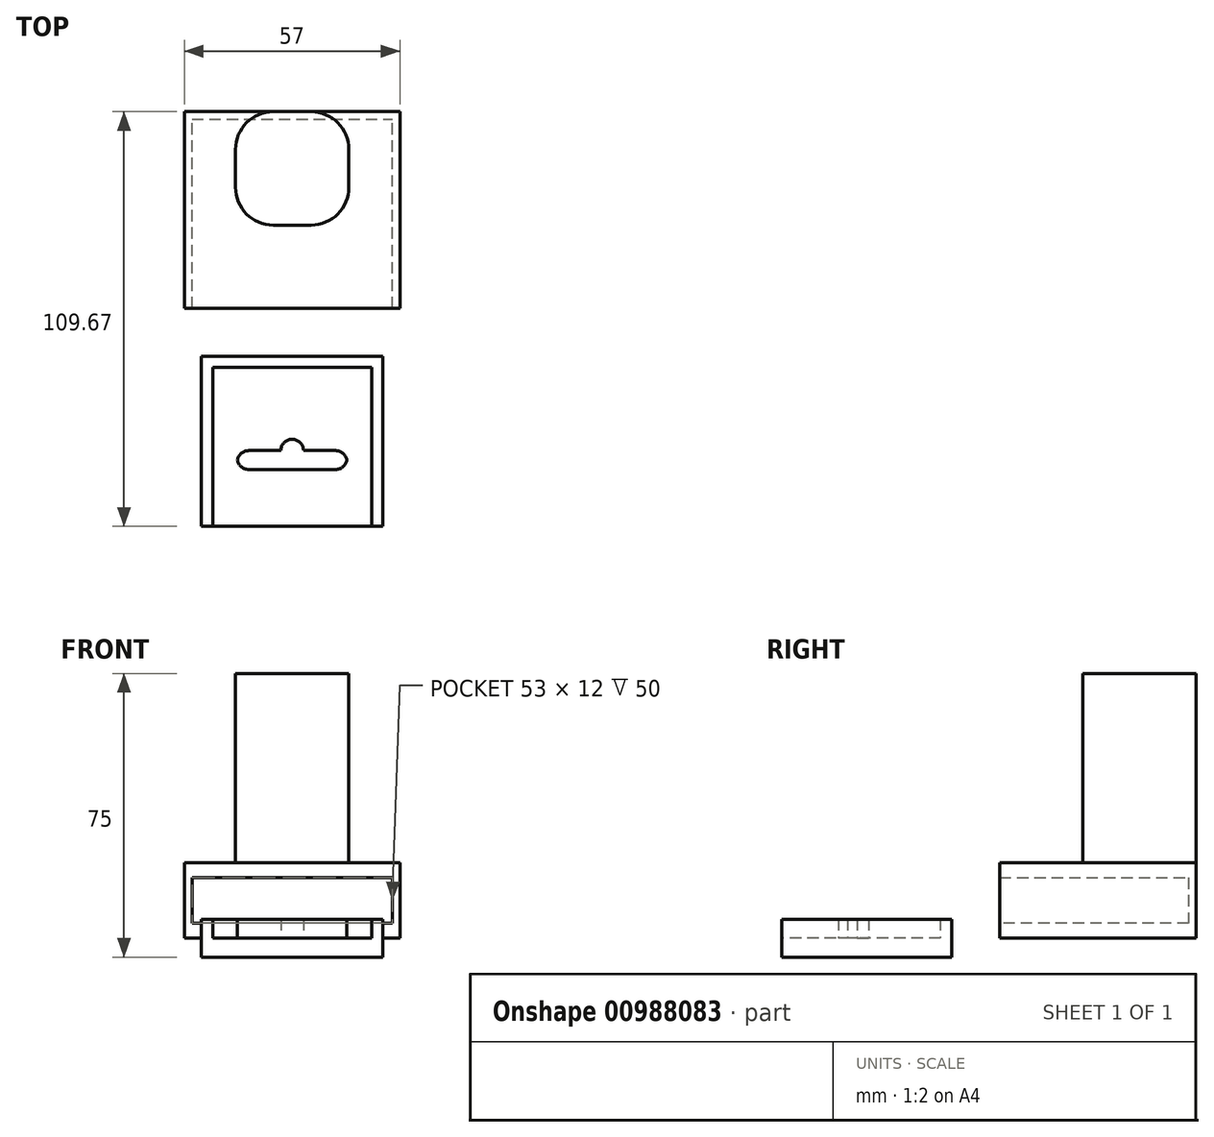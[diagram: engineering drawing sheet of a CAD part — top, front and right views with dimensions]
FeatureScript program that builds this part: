
annotation { "Feature Type Name" : "Feature", "Feature Type Description" : "" }
export const myFeature = defineFeature(function(context is Context, id is Id, definition is map)
    precondition{}
    {
        {
            var Q0;
            Q0=qCreatedBy(makeId("Top.planeOp"),FACE);
            var sketch = newSketch(context, id + "F0", { "sketchPlane" : qUnion([Q0])});
            skLineSegment(sketch, "E0.bottom", {"start": v(21, 19.5) * mm, "end": v(-21, 19.5) * mm});
            skLineSegment(sketch, "E0.top", {"start": v(21, -19.5) * mm, "end": v(-21, -19.5) * mm});
            skLineSegment(sketch, "E0.left", {"start": v(21, 19.5) * mm, "end": v(21, -19.5) * mm});
            skLineSegment(sketch, "E0.right", {"start": v(-21, 19.5) * mm, "end": v(-21, -19.5) * mm});
            skPoint(sketch, "E0.middle", {"position": v(0, 0) * mm});
            skLineSegment(sketch, "E1.bottom", {"start": v(-14.5, -2.5) * mm, "end": v(-3, -2.5) * mm});
            skLineSegment(sketch, "E1.top", {"start": v(-14.5, -7.5) * mm, "end": v(14.5, -7.5) * mm});
            skLineSegment(sketch, "E1.left", {"start": v(-14.5, -2.5) * mm, "end": v(-14.5, -7.5) * mm});
            skLineSegment(sketch, "E1.right", {"start": v(14.5, -2.5) * mm, "end": v(14.5, -7.5) * mm});
            skPoint(sketch, "E2", {"position": v(0, -2.5) * mm});
            skLineSegment(sketch, "E3.bottom", {"start": v(-3, -7.5) * mm, "end": v(3, -7.5) * mm});
            skLineSegment(sketch, "E3.top", {"start": v(-3, 0.5) * mm, "end": v(3, 0.5) * mm});
            skLineSegment(sketch, "E3.left", {"start": v(-3, -2.5) * mm, "end": v(-3, 0.5) * mm});
            skLineSegment(sketch, "E3.right", {"start": v(3, -2.5) * mm, "end": v(3, 0.5) * mm});
            skPoint(sketch, "E4", {"position": v(0, 0.5) * mm});
            skLineSegment(sketch, "E5.trimOffspring", {"start": v(3, -2.5) * mm, "end": v(14.5, -2.5) * mm});
            skLineSegment(sketch, "E6.0", {"start": v(24, 22.5) * mm, "end": v(-24, 22.5) * mm});
            skLineSegment(sketch, "E6.1", {"start": v(24, 22.5) * mm, "end": v(24, -22.5) * mm});
            skLineSegment(sketch, "E6.2", {"start": v(24, -22.5) * mm, "end": v(-24, -22.5) * mm});
            skLineSegment(sketch, "E6.3", {"start": v(-24, 22.5) * mm, "end": v(-24, -22.5) * mm});
            skLineSegment(sketch, "E7", {"start": v(-21, -19.5) * mm, "end": v(-21, -22.5) * mm});
            skLineSegment(sketch, "E8", {"start": v(21, -19.5) * mm, "end": v(21, -22.5) * mm});
            skLineSegment(sketch, "E9.bottom", {"start": v(28.5, 87.17) * mm, "end": v(-28.5, 87.17) * mm});
            skLineSegment(sketch, "E9.top", {"start": v(28.5, 35.17) * mm, "end": v(-28.5, 35.17) * mm});
            skLineSegment(sketch, "E9.left", {"start": v(28.5, 87.17) * mm, "end": v(28.5, 35.17) * mm});
            skLineSegment(sketch, "E9.right", {"start": v(-28.5, 87.17) * mm, "end": v(-28.5, 35.17) * mm});
            skPoint(sketch, "E9.middle", {"position": v(0, 61.17) * mm});
            skLineSegment(sketch, "E10.0", {"start": v(-26.5, 85.17) * mm, "end": v(-26.5, 35.17) * mm});
            skLineSegment(sketch, "E10.1", {"start": v(26.5, 85.17) * mm, "end": v(-26.5, 85.17) * mm});
            skLineSegment(sketch, "E10.2", {"start": v(26.5, 85.17) * mm, "end": v(26.5, 35.17) * mm});
            skSolve(sketch);
        }
        {
            var Q0;
            Q0=makeQuery(id+"F0.imprint","IMPRINT",FACE,{"disambiguationData":[TD([[makeQuery(id+"F0.imprint","IMPRINT",EDGE,{"derivedFrom":sQuery(id+"F0.wireOp",EDGE,"E0.bottom")}),1.0]])]});
            var Q1;
            Q1=makeQuery(id+"F0.imprint","IMPRINT",FACE,{"disambiguationData":[TD([[makeQuery(id+"F0.imprint","IMPRINT",EDGE,{"derivedFrom":sQuery(id+"F0.wireOp",EDGE,"E0.bottom")}),-1.0]])]});
            var Q2;
            Q2=makeQuery(id+"F0.imprint","IMPRINT",FACE,{"disambiguationData":[TD([[makeQuery(id+"F0.imprint","IMPRINT",EDGE,{"derivedFrom":sQuery(id+"F0.wireOp",EDGE,"E0.top")}),1.0]])]});
            var Q3;
            Q3=makeQuery(id+"F0.imprint","IMPRINT",FACE,{"disambiguationData":[TD([[makeQuery(id+"F0.imprint","IMPRINT",EDGE,{"derivedFrom":sQuery(id+"F0.wireOp",EDGE,"E1.bottom")}),-1.0]])]});
            extrude(context, id + "F1", {"entities" : qUnion([Q0, Q1, Q2, Q3]), "oppositeDirection" : true, "depth" : 5 * mm, "offsetDistance" : 25 * mm});
        }
        {
            var Q0;
            Q0=makeQuery(id+"F0.imprint","IMPRINT",FACE,{"disambiguationData":[TD([[makeQuery(id+"F0.imprint","IMPRINT",EDGE,{"derivedFrom":sQuery(id+"F0.wireOp",EDGE,"E1.bottom")}),-1.0]])]});
            var Q1;
            Q1=makeQuery(id+"F0.imprint","IMPRINT",FACE,{"disambiguationData":[TD([[makeQuery(id+"F0.imprint","IMPRINT",EDGE,{"derivedFrom":sQuery(id+"F0.wireOp",EDGE,"E0.bottom")}),-1.0]])]});
            extrude(context, id + "F2", {"entities" : qUnion([Q0, Q1]), "operationType" : NewBodyOperationType.ADD, "depth" : 5 * mm, "offsetDistance" : 25 * mm});
        }
        {
            var Q0;
            Q0=makeQuery(id+"F2.opExtrude","SWEPT_EDGE",EDGE,{"disambiguationData":[OSD([sQuery(id+"F0.wireOp",EDGE,"E3.top"),sQuery(id+"F0.wireOp",EDGE,"E3.left")])]});
            var Q1;
            Q1=makeQuery(id+"F2.opExtrude","SWEPT_EDGE",EDGE,{"disambiguationData":[OSD([sQuery(id+"F0.wireOp",EDGE,"E3.top"),sQuery(id+"F0.wireOp",EDGE,"E3.right")])]});
            var Q2;
            Q2=makeQuery(id+"F2.opExtrude","SWEPT_EDGE",EDGE,{"disambiguationData":[OSD([sQuery(id+"F0.wireOp",EDGE,"E1.bottom"),sQuery(id+"F0.wireOp",EDGE,"E1.left")])]});
            var Q3;
            Q3=makeQuery(id+"F2.opExtrude","SWEPT_EDGE",EDGE,{"disambiguationData":[OSD([sQuery(id+"F0.wireOp",EDGE,"E1.top"),sQuery(id+"F0.wireOp",EDGE,"E1.left")])]});
            var Q4;
            Q4=makeQuery(id+"F2.opExtrude","SWEPT_EDGE",EDGE,{"disambiguationData":[OSD([sQuery(id+"F0.wireOp",EDGE,"E1.right"),sQuery(id+"F0.wireOp",EDGE,"E5.trimOffspring")])]});
            var Q5;
            Q5=makeQuery(id+"F2.opExtrude","SWEPT_EDGE",EDGE,{"disambiguationData":[OSD([sQuery(id+"F0.wireOp",EDGE,"E1.top"),sQuery(id+"F0.wireOp",EDGE,"E1.right")])]});
            fillet(context, id + "F3", {"entities" : qUnion([Q0, Q1, Q2, Q3, Q4, Q5]), "radius" : 3 * mm, "tangentPropagation" : true, "allowEdgeOverflow" : false});
        }
        {
            var Q0;
            Q0=makeQuery(id+"F0.imprint","IMPRINT",FACE,{"disambiguationData":[TD([[makeQuery(id+"F0.imprint","IMPRINT",EDGE,{"derivedFrom":sQuery(id+"F0.wireOp",EDGE,"E9.bottom")}),1.0]])]});
            extrude(context, id + "F4", {"entities" : qUnion([Q0]), "depth" : 20 * mm, "offsetDistance" : 25 * mm});
        }
        {
            var Q0;
            {var subQ0=sQuery(id+"F0.wireOp",EDGE,"E10.0");Q0=makeQuery(id+"F0.imprint","IMPRINT",FACE,{"disambiguationData":[TD([[makeQuery(id+"F0.imprint","IMPRINT",EDGE,{"derivedFrom":subQ0}),1.0]])]});}
            extrude(context, id + "F5", {"entities" : qUnion([Q0]), "operationType" : NewBodyOperationType.ADD, "depth" : 4 * mm, "offsetDistance" : 25 * mm});
        }
        {
            var Q0;
            Q0=makeQuery(id+"F4.opExtrude","SWEPT_FACE",FACE,{"disambiguationData":[OSD([sQuery(id+"F0.wireOp",EDGE,"E10.1")])]});
            var sketch = newSketch(context, id + "F6", { "sketchPlane" : qUnion([Q0])});
            skLineSegment(sketch, "E11", {"start": v(-26.5, 16) * mm, "end": v(26.5, 16) * mm});
            skSolve(sketch);
        }
        {
            var Q0;
            {var subQ0=sQuery(id+"F6.wireOp",EDGE,"E11");Q0=makeQuery(id+"F6.imprint","IMPRINT",FACE,{"disambiguationData":[TD([[makeQuery(id+"F6.imprint","IMPRINT",EDGE,{"derivedFrom":subQ0}),1.0]])]});}
            extrude(context, id + "F7", {"entities" : qUnion([Q0]), "operationType" : NewBodyOperationType.ADD, "depth" : 50 * mm, "offsetDistance" : 25 * mm});
        }
        {
            var Q0;
            {var subQ0=sQuery(id+"F0.wireOp",EDGE,"E10.1");Q0=makeQuery(id+"F7.boolean.opBoolean","MERGE",FACE,{"derivedFrom":[makeQuery(id+"F4.opExtrude","CAP_FACE",FACE,{"disambiguationData":[OSD([sQuery(id+"F0.wireOp",EDGE,"E9.bottom"),sQuery(id+"F0.wireOp",EDGE,"E9.top"),sQuery(id+"F0.wireOp",EDGE,"E9.left"),sQuery(id+"F0.wireOp",EDGE,"E9.right"),sQuery(id+"F0.wireOp",EDGE,"E10.0"),subQ0,sQuery(id+"F0.wireOp",EDGE,"E10.2")])],"isStart":false}),makeQuery(id+"F7.opExtrude","SWEPT_FACE",FACE,{"disambiguationData":[OSD([subQ0])]})]});}
            var sketch = newSketch(context, id + "F8", { "sketchPlane" : qUnion([Q0])});
            skLineSegment(sketch, "E12.bottom", {"start": v(-15, 87.17) * mm, "end": v(15, 87.17) * mm});
            skLineSegment(sketch, "E12.top", {"start": v(-15, 57.17) * mm, "end": v(15, 57.17) * mm});
            skLineSegment(sketch, "E12.left", {"start": v(-15, 87.17) * mm, "end": v(-15, 57.17) * mm});
            skLineSegment(sketch, "E12.right", {"start": v(15, 87.17) * mm, "end": v(15, 57.17) * mm});
            skPoint(sketch, "E13", {"position": v(0, 87.17) * mm});
            skPoint(sketch, "E14", {"position": v(0, 57.17) * mm});
            skSolve(sketch);
        }
        {
            var Q0;
            Q0=makeQuery(id+"F8.imprint","IMPRINT",FACE,{"disambiguationData":[TD([[makeQuery(id+"F8.imprint","IMPRINT",EDGE,{"derivedFrom":sQuery(id+"F8.wireOp",EDGE,"E12.bottom")}),1.0]])]});
            extrude(context, id + "F9", {"entities" : qUnion([Q0]), "operationType" : NewBodyOperationType.ADD, "depth" : 50 * mm, "offsetDistance" : 25 * mm});
        }
        {
            var Q0;
            Q0=makeQuery(id+"F9.opExtrude","SWEPT_EDGE",EDGE,{"disambiguationData":[OSD([sQuery(id+"F8.wireOp",EDGE,"E12.top"),sQuery(id+"F8.wireOp",EDGE,"E12.right")])]});
            var Q1;
            Q1=makeQuery(id+"F9.opExtrude","SWEPT_EDGE",EDGE,{"disambiguationData":[OSD([sQuery(id+"F8.wireOp",EDGE,"E12.top"),sQuery(id+"F8.wireOp",EDGE,"E12.left")])]});
            var Q2;
            Q2=makeQuery(id+"F9.opExtrude","SWEPT_EDGE",EDGE,{"disambiguationData":[OSD([sQuery(id+"F0.wireOp",EDGE,"E9.bottom"),sQuery(id+"F8.wireOp",EDGE,"E12.bottom"),sQuery(id+"F8.wireOp",EDGE,"E12.left")])]});
            var Q3;
            Q3=makeQuery(id+"F9.opExtrude","SWEPT_EDGE",EDGE,{"disambiguationData":[OSD([sQuery(id+"F0.wireOp",EDGE,"E9.bottom"),sQuery(id+"F8.wireOp",EDGE,"E12.bottom"),sQuery(id+"F8.wireOp",EDGE,"E12.right")])]});
            fillet(context, id + "F10", {"entities" : qUnion([Q0, Q1, Q2, Q3]), "radius" : 10 * mm, "tangentPropagation" : true, "allowEdgeOverflow" : false});
        }
    });
